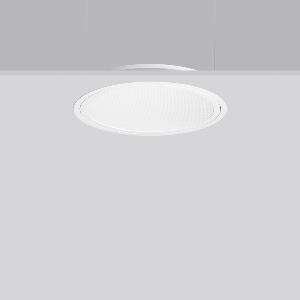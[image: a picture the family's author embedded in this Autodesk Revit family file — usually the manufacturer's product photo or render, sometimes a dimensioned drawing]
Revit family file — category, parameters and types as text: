
# Revit family: triona_round_e_312423_002_1_12_c71b
name_source: partatom
category: Lighting Fixtures
units: mm (PartAtom-declared; Revit-internal decimal feet)

## family parameters
Cut with Voids When Loaded = No
Host = Face
Light Source = No
Part Type = Normal
Room Calculation Point = No
Round Connector Dimension = Use Diameter
Shared = No

## types (1)
- TRIONA round E (1 x LED Modul 840, 3250 lm, 4000)
    Apparent Load = 28 VA
    CIE Flux Codes = 58 87 97 100 100
    Color Rendering = 80
    Color Temperature = 4000
    Default Elevation = 1800 mm
    Description = Series: TRIONA round
Decorative round LED recessed surface luminaire. Cover made of sheet steel, powder-coated. Frame made of aluminium, powder-coated. Recessed ring: aluminium extrusion profile, powder coated. Light emission through a diffuser in plastic, opal/prismatic. Lightguide and diffuser made of non-yellowing plastic (PMMA). Lateral light emission (RZB SIDELITE technology) for above-average homogeneous light distribution. Suitable for installation in cavity ceilings. Tool-free mounting system thanks to the rocker arm mechanism (patent pending). Electronic ballast included. Very easy installation thanks to Plug+Play connection. 
Colour: traffic white, matt (RAL 9016)
Diameter: 505 mm
Height: 2 mm
Cut-out diameter: 482 mm
Recess height: 100 mm
Luminaire: recess height: 89 mm
Lamp: LED
Socket: without socket
Colour temperature: 4000K
Colour rendering index (CRI): 80
System power: 28 W
Rated luminous flux: 3250 lm
Luminous efficiency: 116 lm/W
Control gear: Converter, dimmable, DALI
Protection class: I
Type of protection: IP 40
    Height = 0 mm  [stored 0 ft]
    Lamp = 1 x LED Modul 840
    Lamp Light Flux = 3250 lm
    Lamp count = 1
    Length = 505 mm
    Lifetime = 50000 h
    Luminous efficacy = 116 lm/W
    Manufacturer = RZB
    ModVariant = No
    Model = 312423.002.1.12
    Mounting Place = Ceiling
    Mounting Type = Recessed
    Number of Poles = 1
    OnlyDefault = Yes
    Power Factor = 1
    Product Name = TRIONA round E
    Product group = Recessed modular luminaires
    ProductGroupID = 406
    Protection Class = Protection class I
    Protection Degree = IP 20
    RLX_Detail_Level = 1
    RLX_Emergency_Light_Flux = 0 lm
    RLX_Emergency_Type = 0
    RLX_Emergency_Type_DB = No
    RlxData = <blob elided: 30789 chars, md5=09b8b778>
    Socket = socket
    Standby Power = 0 W
    System Light Flux = 3250 lm
    System Power = 28 W
    Type Comments = Product without accessories
    Type Image = 312423.002.12.jpg
    URL = http://relux.com
    VarID = ---
    Voltage = 230 V
    Voltage Range = 220-240 V
    Weight = 0.00 kg
    Width = 0 mm  [stored 0 ft]

note: [stored X ft] marks values corroborated as IEEE doubles in the binary element streams (Revit-internal decimal feet)

## geometry (parser evidence)
native form markers: Blend x4, Sweep x8
no freeform markers — native parametric forms only
